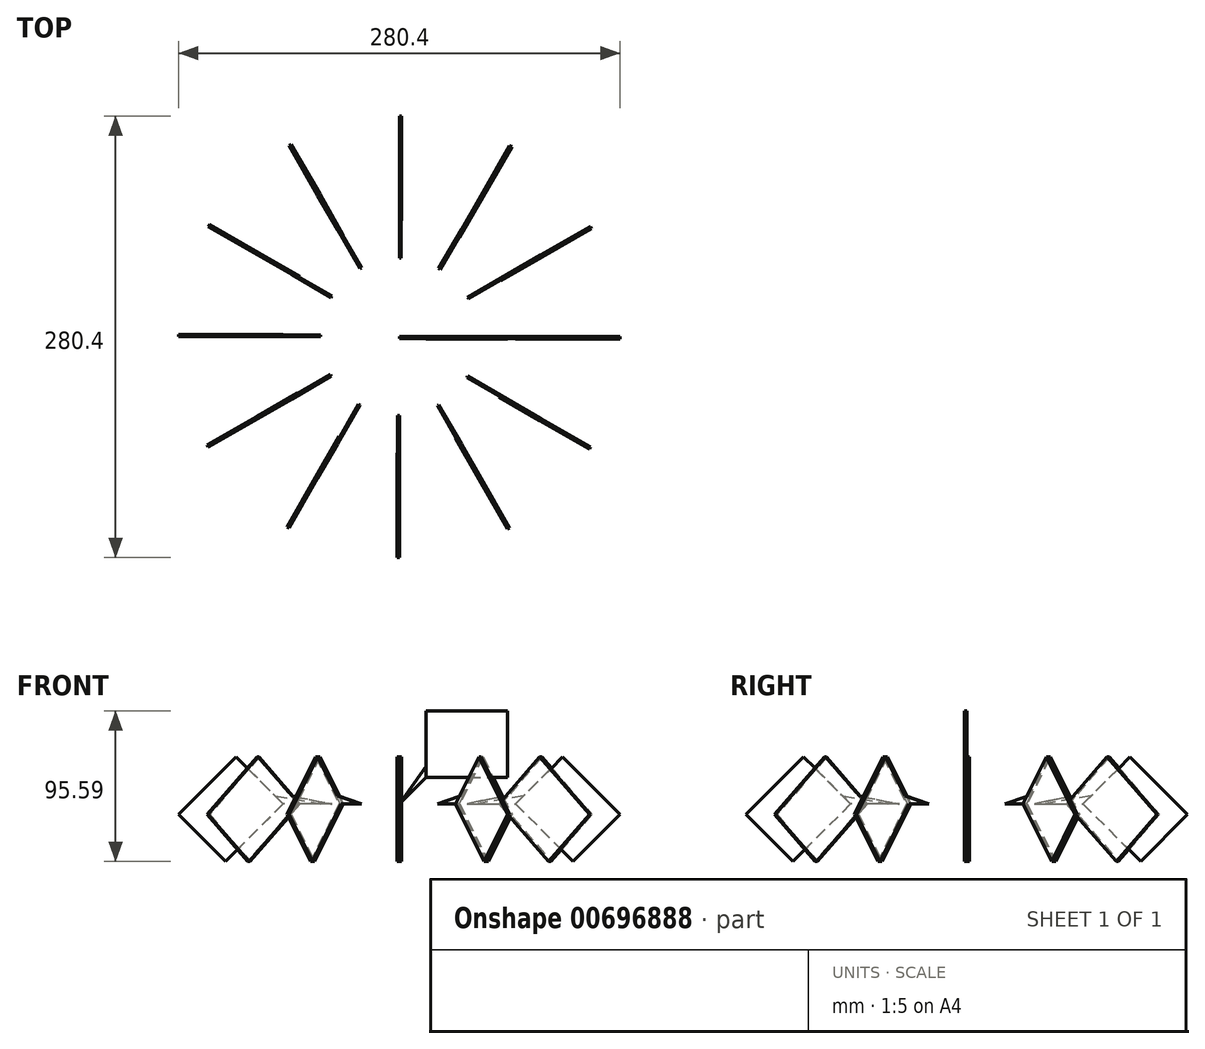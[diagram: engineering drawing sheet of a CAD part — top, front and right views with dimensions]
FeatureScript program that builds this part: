
annotation { "Feature Type Name" : "Feature", "Feature Type Description" : "" }
export const myFeature = defineFeature(function(context is Context, id is Id, definition is map)
    precondition{}
    {
        {
            var Q0;
            Q0=qCreatedBy(makeId("Front.planeOp"),FACE);
            var sketch = newSketch(context, id + "F0", { "sketchPlane" : qUnion([Q0])});
            skLineSegment(sketch, "E0.bottom", {"start": v(16.91, 58.94) * mm, "end": v(68.62, 58.94) * mm});
            skLineSegment(sketch, "E0.top", {"start": v(16.91, 16.79) * mm, "end": v(68.62, 16.79) * mm});
            skLineSegment(sketch, "E0.left", {"start": v(16.91, 58.94) * mm, "end": v(16.91, 23.83) * mm});
            skLineSegment(sketch, "E0.right", {"start": v(68.62, 58.94) * mm, "end": v(68.62, 16.79) * mm});
            skLineSegment(sketch, "E1", {"start": v(16.91, 23.83) * mm, "end": v(0, 0) * mm});
            skLineSegment(sketch, "E2", {"start": v(0, 0) * mm, "end": v(16.91, 16.79) * mm});
            skSolve(sketch);
        }
        {
            var Q0;
            Q0 = qSketchRegion(id + "F0", true);
            extrude(context, id + "F1", {"entities" : qUnion([Q0]), "depth" : 1 * mm, "offsetDistance" : 25 * mm});
        }
        {
            var Q0;
            Q0=makeQuery(id+"F1.opExtrude","CAP_FACE",FACE,{"disambiguationData":[OSD([sQuery(id+"F0.wireOp",EDGE,"E0.bottom"),sQuery(id+"F0.wireOp",EDGE,"E0.top"),sQuery(id+"F0.wireOp",EDGE,"E0.left"),sQuery(id+"F0.wireOp",EDGE,"E0.right"),sQuery(id+"F0.wireOp",EDGE,"E1"),sQuery(id+"F0.wireOp",EDGE,"E2")])],"isStart":false});
            var sketch = newSketch(context, id + "F2", { "sketchPlane" : qUnion([Q0])});
            skLineSegment(sketch, "E3", {"start": v(16.91, 23.83) * mm, "end": v(16.91, 16.79) * mm});
            skSolve(sketch);
        }
        {
            var Q0;
            Q0=makeQuery(id+"F2.imprint","IMPRINT",FACE,{"disambiguationData":[TD([[makeQuery(id+"F2.imprint","IMPRINT",EDGE,{"derivedFrom":sQuery(id+"F2.wireOp",EDGE,"E3")}),1.0]])]});
            extrude(context, id + "F3", {"entities" : qUnion([Q0]), "operationType" : NewBodyOperationType.ADD, "depth" : .5 * mm, "offsetDistance" : 25 * mm});
        }
        {
            var Q0;
            Q0=qCreatedBy(makeId("Front.planeOp"),FACE);
            var sketch = newSketch(context, id + "F4", { "sketchPlane" : qUnion([Q0])});
            skLineSegment(sketch, "E4", {"start": v(0, 0) * mm, "end": v(10.42, 0) * mm});
            skLineSegment(sketch, "E5", {"start": v(0, 0) * mm, "end": v(0, 12.66) * mm});
            skSolve(sketch);
        }
        {
            var Q0;
            Q0=qCreatedBy(makeId("Right.planeOp"),FACE);
            var sketch = newSketch(context, id + "F5", { "sketchPlane" : qUnion([Q0])});
            skLineSegment(sketch, "E6", {"start": v(0, 0) * mm, "end": v(-11.57, 0) * mm});
            skSolve(sketch);
        }
        {
            var Q0;
            Q0=makeQuery(id+"F1.opExtrude","SWEPT_BODY",BODY,{"disambiguationData":[OSD([sQuery(id+"F0.wireOp",EDGE,"E0.bottom"),sQuery(id+"F0.wireOp",EDGE,"E0.top"),sQuery(id+"F0.wireOp",EDGE,"E0.left"),sQuery(id+"F0.wireOp",EDGE,"E0.right"),sQuery(id+"F0.wireOp",EDGE,"E1"),sQuery(id+"F0.wireOp",EDGE,"E2")])]});
            var Q1;
            Q1=sQuery(id+"F5.wireOp",EDGE,"E6");
            transform(context, id + "F6", {"entities" : qUnion([Q0]), "transformType" : TransformType.ROTATION, "transformAxis" : qUnion([Q1]), "angle" : 315 * degree, "makeCopy" : true});
        }
        {
            var Q0;
            Q0=makeQuery(id+"F6.opPattern","COPY",BODY,{"derivedFrom":makeQuery(id+"F1.opExtrude","SWEPT_BODY",BODY,{"disambiguationData":[OSD([sQuery(id+"F0.wireOp",EDGE,"E0.bottom"),sQuery(id+"F0.wireOp",EDGE,"E0.top"),sQuery(id+"F0.wireOp",EDGE,"E0.left"),sQuery(id+"F0.wireOp",EDGE,"E0.right"),sQuery(id+"F0.wireOp",EDGE,"E1"),sQuery(id+"F0.wireOp",EDGE,"E2")])]}),"instanceName":"1"});
            transform(context, id + "F7", {"entities" : qUnion([Q0]), "transformType" : TransformType.TRANSLATION_3D, "dx" : 50 * mm, "dy" : 0 * mm, "dz" : 0 * mm, "makeCopy" : false});
        }
        {
            var Q0;
            Q0=makeQuery(id+"F6.opPattern","COPY",BODY,{"derivedFrom":makeQuery(id+"F1.opExtrude","SWEPT_BODY",BODY,{"disambiguationData":[OSD([sQuery(id+"F0.wireOp",EDGE,"E0.bottom"),sQuery(id+"F0.wireOp",EDGE,"E0.top"),sQuery(id+"F0.wireOp",EDGE,"E0.left"),sQuery(id+"F0.wireOp",EDGE,"E0.right"),sQuery(id+"F0.wireOp",EDGE,"E1"),sQuery(id+"F0.wireOp",EDGE,"E2")])]}),"instanceName":"1"});
            var Q1;
            Q1=sQuery(id+"F4.wireOp",EDGE,"E5");
            circularPattern(context, id + "F8", {"entities" : qUnion([Q0]), "axis" : qUnion([Q1]), "angle" : 360 * degree, "instanceCount" : 12, "equalSpace" : true});
        }
    });
